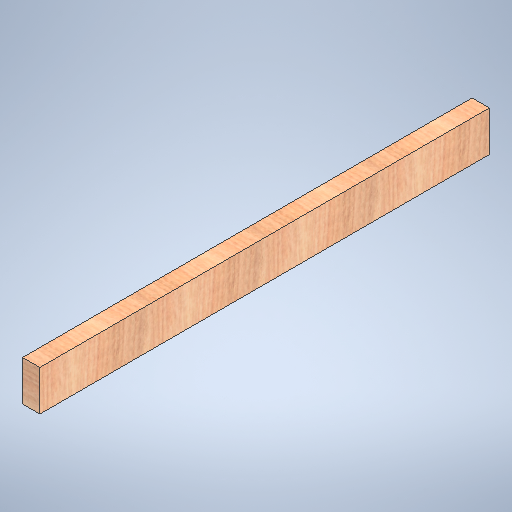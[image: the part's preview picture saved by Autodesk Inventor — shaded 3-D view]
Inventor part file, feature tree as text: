
AUTODESK INVENTOR PART (.ipt)
format: ipt  version: 2025.1 (Build 291241020, 241B)  size: 327,680 bytes
history: native  units: in
note: dims shown in document units (in); Inventor stores cm internally (conversion verified against a paired STEP export)
features: extrude x1, sketch x1
ambient origin geometry x8: Origin, YZ Plane, XZ Plane, XY Plane, X Axis, Y Axis, Z Axis, Center Point
bodies: Solid1 (feature_tree)
feature tree (2):
  extrude  "Extrusion1"  Depth=1.5in TaperAngle=0.0deg
  sketch  "Sketch1"  dims[d1=39.0in d2=1.5in d3=0.0in d4=3.5in]
